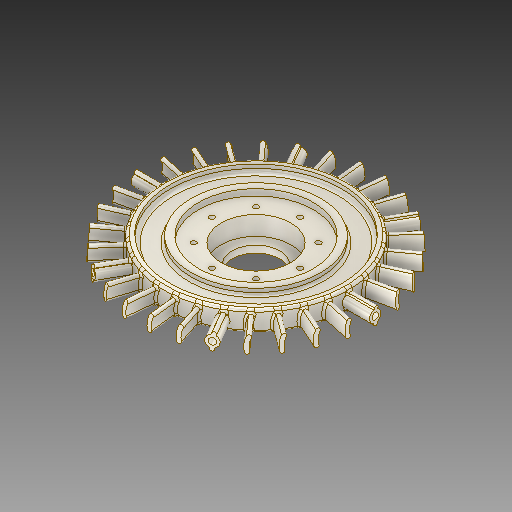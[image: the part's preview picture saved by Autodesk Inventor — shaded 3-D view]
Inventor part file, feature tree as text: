
AUTODESK INVENTOR PART (.ipt)
format: ipt  version: 2019 (Build 230136000, 136)  size: 3,207,680 bytes
history: native  units: mm
features: sketch x10, extrude x9, fillet x7, hole x6, pattern_circular x3, direct_edit x1, projected_geometry x1, move_body x1
ambient origin geometry x8: Origin, YZ Plane, XZ Plane, XY Plane, X Axis, Y Axis, Z Axis, Center Point
bodies: Solid1 (feature_tree)
feature tree (38):
  extrude  "Extrusion1"  Depth=15.5mm TaperAngle=0.0deg
  extrude  "Extrusion2"  Depth=300.0mm TaperAngle=0.0deg
  fillet  "Fillet2"  Radius=190.0mm
  pattern_circular  "Circular Pattern2"  Count=30 Angle=360.0deg
  extrude  "Extrusion6"  Depth=3.0mm
  hole  "Hole5"  [1 undecoded]
  pattern_circular  "Circular Pattern3"  Count=6 Angle=360.0deg
  extrude  "Extrusion3"  Depth=3.0mm
  hole  "Hole6"  [1 undecoded]
  fillet  "Fillet11"  Radius=102.5mm
  extrude  "Extrusion7"  Depth=5.0mm TaperAngle=0.0deg
  fillet  "Fillet12"  Radius=2.0mm
  hole  "Hole7"  [1 undecoded]
  extrude  "Extrusion8"  Depth=35.0mm
  extrude  "Extrusion9"  Depth=80.0mm TaperAngle=360.0deg
  hole  "Hole8"  [1 undecoded]
  extrude  "Extrusion10"  Depth=10.0mm TaperAngle=0.0deg
  fillet  "Fillet13"  Radius=50.0mm
  pattern_circular  "Circular Pattern4"  [2 undecoded]
  direct_edit  "Direct Edit1"
  fillet  "Fillet14"  Radius=10.0mm
  fillet  "Fillet15"  Radius=135.0mm
  hole  "Hole9"  [1 undecoded]
  hole  "Hole10"  [1 undecoded]
  extrude  "Extrusion11"  Depth=2.0mm
  fillet  "Fillet16"  Radius=15.0mm
  sketch  "Sketch1"  dims[d0=146.0mm d1=15.5mm d2=0.0mm]
  sketch  "Sketch3"  dims[d33=3.0mm d34=300.0mm d35=0.0mm d36=190.0mm]
  sketch  "Sketch4"  dims[d37=111.0mm d38=-0.523599mm d39=300.0mm d40=360.0deg]
  sketch  "Sketch8"  dims[d42=1.5mm d61=3.0mm]
  sketch  "Sketch9"  dims[d62=10.0mm d97=9.0mm]
  sketch  "Sketch10"  dims[d98=7.5mm]
  sketch  "Sketch11"  dims[d99=305.25mm d100=0.0mm]
  sketch  "Sketch12"  dims[d183=10.0mm d184=10.0mm d103=5.0mm d104=6.0mm d105=4.0mm d106=2.0mm d107=90.0deg d108=227.75mm d109=20.594885mm d110=60.0mm d111=360.0deg]
  sketch  "Sketch13"  dims[d113=10.0mm d114=10.0mm]
  sketch  "Sketch14"  dims[d115=136.0mm d116=6.0mm d117=4.0mm d118=2.0mm d119=90.0deg d120=5.0mm d121=0.0mm d122=3.0mm d123=91.0mm d124=102.5mm d125=5.0mm d126=0.0mm d127=2.0mm d128=45.0deg d129=35.0mm d130=4.2mm d131=6.0mm d132=4.0mm d133=2.0mm d134=90.0deg d135=5.0mm d136=0.0mm d137=80.0mm d138=360.0deg d140=15.0mm d141=10.0mm d142=0.0mm d143=50.0mm d144=10.0mm d145=0.0mm d146=10.0mm d147=10.0mm d148=38.0mm d149=6.0mm d150=4.0mm d151=2.0mm d152=90.0deg d153=5.0mm d154=0.0mm d155=135.0mm d156=104.0mm d157=3.0mm d158=0.0mm d159=2.0mm d160=15.0mm d161=4.0mm d162=0.0mm d163=0.0mm d164=20.0mm d165=10.0mm d166=10.0mm d167=60.0mm d168=6.0mm d169=4.0mm d170=2.0mm d171=90.0deg d172=20.0mm d173=0.0mm d174=10.0mm d175=10.0mm d176=55.0mm d177=6.0mm d178=4.0mm d179=2.0mm d180=90.0deg d181=20.0mm d182=0.0mm d185=1.0mm d186=0.0mm d187=2.0mm]
  projected_geometry  "Projected Loop1"
  move_body  "Move1"
note: 8 required parameter values undecoded (feature->parameter linkage not recoverable at this tier; creation-order binding heuristic only, values carry confidence <= 0.55)
